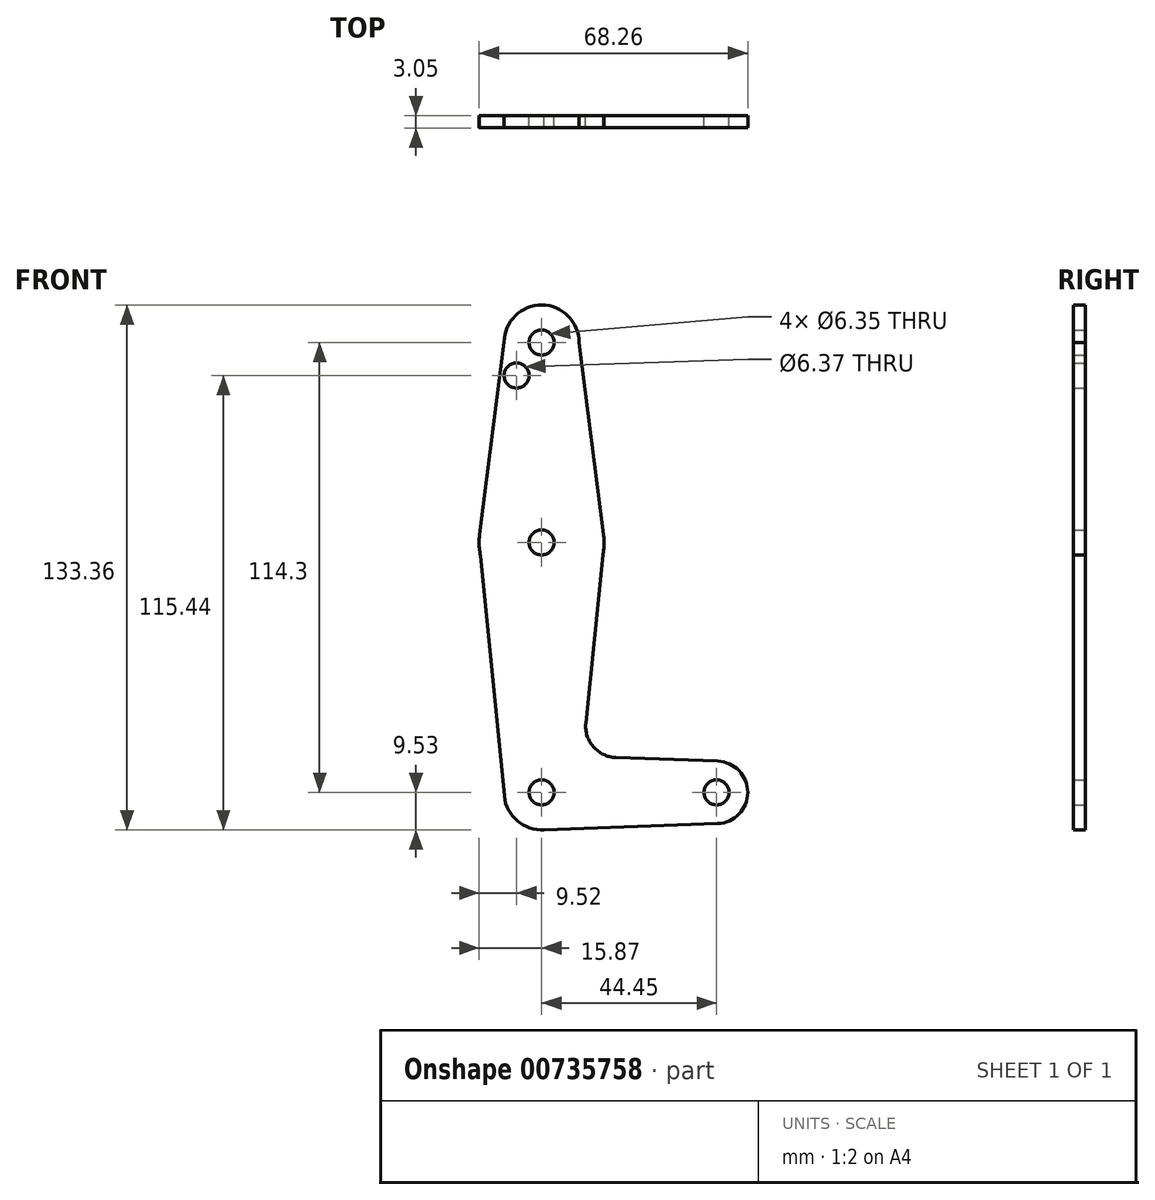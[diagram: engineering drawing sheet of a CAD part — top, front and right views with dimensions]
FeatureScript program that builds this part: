
annotation { "Feature Type Name" : "Feature", "Feature Type Description" : "" }
export const myFeature = defineFeature(function(context is Context, id is Id, definition is map)
    precondition{}
    {
        {
            var Q0;
            Q0=qCreatedBy(makeId("Front.planeOp"),FACE);
            var sketch = newSketch(context, id + "F0", { "sketchPlane" : qUnion([Q0])});
            skLineSegment(sketch, "E0", {"start": v(0, 0) * mm, "end": v(0, 114.3) * mm, "construction": true});
            skLineSegment(sketch, "E1", {"start": v(0, 0) * mm, "end": v(44.45, 0) * mm, "construction": true});
            skCircle(sketch, "E2", {"center": v(0, 114.3) * mm, "radius": 9.53 * mm});
            skCircle(sketch, "E3", {"center": v(0, 0) * mm, "radius": 9.53 * mm});
            skCircle(sketch, "E4", {"center": v(44.45, 0) * mm, "radius": 7.94 * mm});
            skCircle(sketch, "E5", {"center": v(0, 63.5) * mm, "radius": 15.88 * mm});
            skLineSegment(sketch, "E6", {"start": v(-9.52, 114.43) * mm, "end": v(-15.75, 65.5) * mm});
            skLineSegment(sketch, "E7", {"start": v(9.52, 114.3) * mm, "end": v(15.75, 65.5) * mm});
            skLineSegment(sketch, "E8", {"start": v(-15.87, 63.76) * mm, "end": v(-9.48, -0.94) * mm});
            skLineSegment(sketch, "E9", {"start": v(15.88, 63.5) * mm, "end": v(11.25, 17.6) * mm});
            skLineSegment(sketch, "E10", {"start": v(18.87, 8.85) * mm, "end": v(44.73, 7.93) * mm});
            skLineSegment(sketch, "E11", {"start": v(0, -9.53) * mm, "end": v(44.73, -7.93) * mm});
            skCircle(sketch, "E12", {"center": v(0, 114.3) * mm, "radius": 3.18 * mm});
            skCircle(sketch, "E13", {"center": v(0, 63.5) * mm, "radius": 3.18 * mm});
            skCircle(sketch, "E14", {"center": v(0, 0) * mm, "radius": 3.18 * mm});
            skCircle(sketch, "E15", {"center": v(44.45, 0) * mm, "radius": 3.18 * mm});
            skCircle(sketch, "E16", {"center": v(-6.35, 105.91) * mm, "radius": 3.18 * mm});
            skPoint(sketch, "E17.newPointB", {"position": v(0, 9.52) * mm});
            skArc(sketch, "E17.filletArc", {"start": v(11.25, 17.6) * mm, "mid": v(13.17, 11.57) * mm, "end": v(18.87, 8.85) * mm});
            skSolve(sketch);
        }
        {
            var Q0;
            Q0 = qSketchRegion(id + "F0", true);
            extrude(context, id + "F1", {"entities" : qUnion([Q0]), "depth" : 3.05 * mm, "offsetDistance" : 25.4 * mm});
        }
    });
